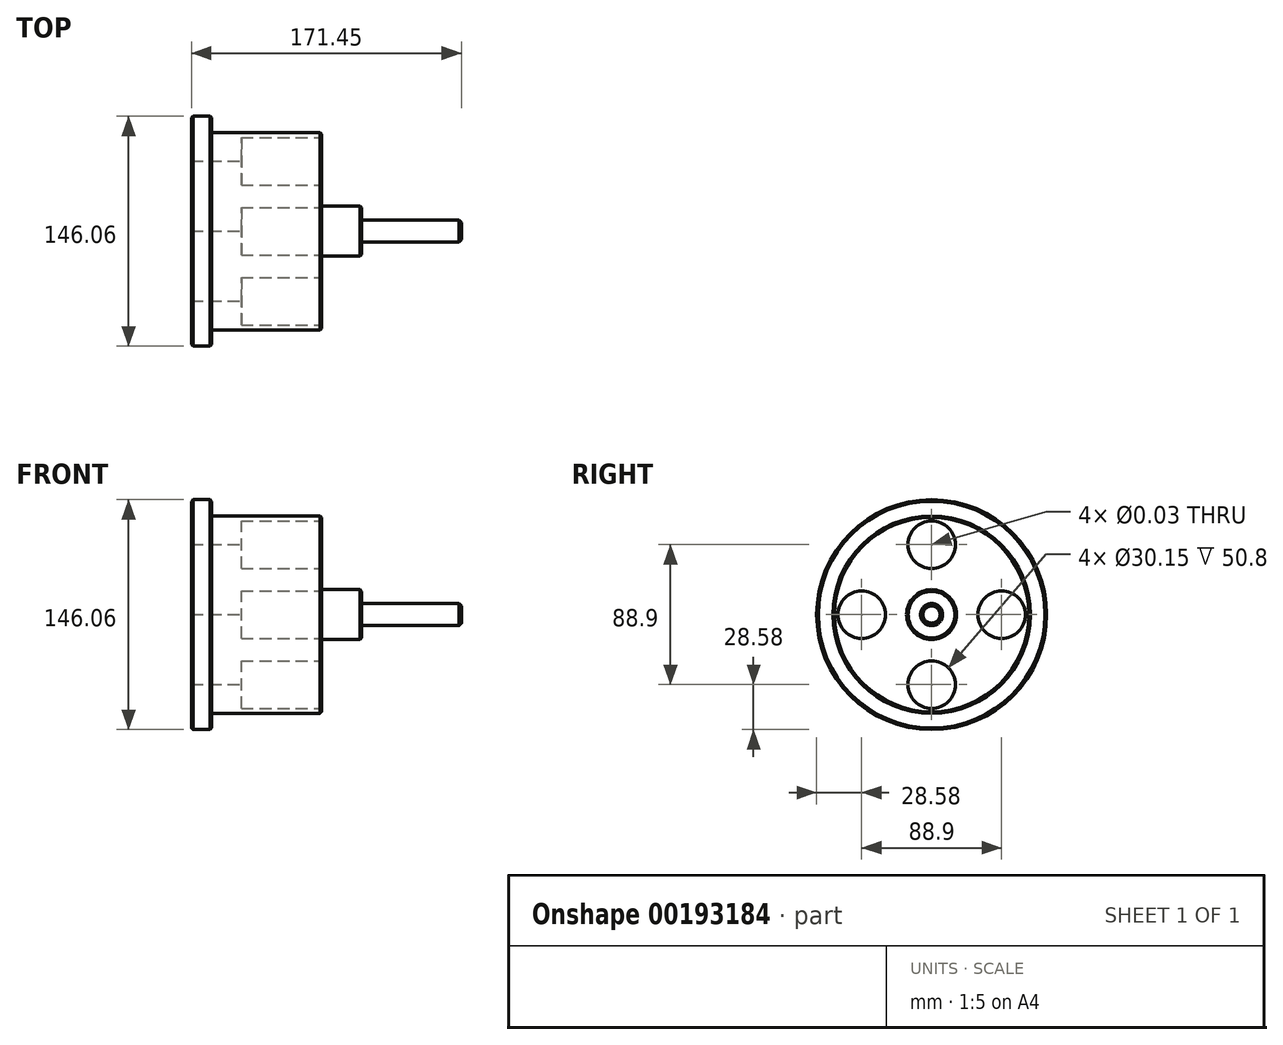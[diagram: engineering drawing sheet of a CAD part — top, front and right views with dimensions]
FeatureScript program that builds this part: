
annotation { "Feature Type Name" : "Feature", "Feature Type Description" : "" }
export const myFeature = defineFeature(function(context is Context, id is Id, definition is map)
    precondition{}
    {
        {
            var Q0;
            Q0=qCreatedBy(makeId("Right.planeOp"),FACE);
            var sketch = newSketch(context, id + "F0", { "sketchPlane" : qUnion([Q0])});
            skCircle(sketch, "E0", {"center": v(0, 0) * mm, "radius": 73.03 * mm});
            skSolve(sketch);
        }
        {
            var Q0;
            Q0 = qSketchRegion(id + "F0", true);
            extrude(context, id + "F1", {"entities" : qUnion([Q0]), "depth" : 12.7 * mm});
        }
        {
            var Q0;
            Q0=makeQuery(id+"F1.opExtrude","CAP_FACE",FACE,{"disambiguationData":[OSD([sQuery(id+"F0.wireOp",EDGE,"E0")])],"isStart":false});
            var sketch = newSketch(context, id + "F2", { "sketchPlane" : qUnion([Q0])});
            skCircle(sketch, "E1", {"center": v(0, 0) * mm, "radius": 62.7 * mm});
            skSolve(sketch);
        }
        {
            var Q0;
            Q0 = qSketchRegion(id + "F2", true);
            extrude(context, id + "F3", {"entities" : qUnion([Q0]), "operationType" : NewBodyOperationType.ADD, "depth" : 69.85 * mm});
        }
        {
            var Q0;
            Q0=makeQuery(id+"F3.opExtrude","CAP_FACE",FACE,{"disambiguationData":[OSD([sQuery(id+"F2.wireOp",EDGE,"E1")])],"isStart":false});
            var sketch = newSketch(context, id + "F4", { "sketchPlane" : qUnion([Q0])});
            skCircle(sketch, "E2", {"center": v(0, 0) * mm, "radius": 15.88 * mm});
            skSolve(sketch);
        }
        {
            var Q0;
            Q0 = qSketchRegion(id + "F4", true);
            extrude(context, id + "F5", {"entities" : qUnion([Q0]), "operationType" : NewBodyOperationType.ADD, "depth" : 25.4 * mm});
        }
        {
            var Q0;
            Q0=makeQuery(id+"F5.opExtrude","CAP_FACE",FACE,{"disambiguationData":[OSD([sQuery(id+"F4.wireOp",EDGE,"E2")])],"isStart":false});
            var sketch = newSketch(context, id + "F6", { "sketchPlane" : qUnion([Q0])});
            skCircle(sketch, "E3", {"center": v(0, 0) * mm, "radius": 7 * mm});
            skSolve(sketch);
        }
        {
            var Q0;
            Q0 = qSketchRegion(id + "F6", true);
            extrude(context, id + "F7", {"entities" : qUnion([Q0]), "operationType" : NewBodyOperationType.ADD, "depth" : 63.5 * mm});
        }
        {
            var Q0;
            Q0=makeQuery(id+"F1.opExtrude","SWEPT_FACE",FACE,{"disambiguationData":[OSD([sQuery(id+"F0.wireOp",EDGE,"E0")])]});
            var Q1;
            Q1=makeQuery(id+"F3.opExtrude","CAP_EDGE",EDGE,{"disambiguationData":[OSD([sQuery(id+"F2.wireOp",EDGE,"E1")])],"isStart":false});
            var Q2;
            Q2=makeQuery(id+"F5.opExtrude","CAP_EDGE",EDGE,{"disambiguationData":[OSD([sQuery(id+"F4.wireOp",EDGE,"E2")])],"isStart":false});
            chamfer(context, id + "F8", {"entities" : qUnion([Q0, Q1, Q2]), "width" : 1.02 * mm, "tangentPropagation" : true});
        }
        {
            var Q0;
            Q0=makeQuery(id+"F7.opExtrude","CAP_EDGE",EDGE,{"disambiguationData":[OSD([sQuery(id+"F6.wireOp",EDGE,"E3")])],"isStart":false});
            chamfer(context, id + "F9", {"entities" : qUnion([Q0]), "width" : 1.52 * mm, "tangentPropagation" : true});
        }
        {
            var Q0;
            Q0=makeQuery(id+"F3.opExtrude","CAP_FACE",FACE,{"disambiguationData":[OSD([sQuery(id+"F2.wireOp",EDGE,"E1")])],"isStart":false});
            var sketch = newSketch(context, id + "F10", { "sketchPlane" : qUnion([Q0])});
            skCircle(sketch, "E4", {"center": v(0, 0) * mm, "radius": 44.45 * mm, "construction": true});
            skLineSegment(sketch, "E5", {"start": v(0, 0) * mm, "end": v(0, 88.67) * mm, "construction": true});
            skPoint(sketch, "E6", {"position": v(0, 44.45) * mm});
            skPoint(sketch, "E7.1.0", {"position": v(-44.45, 0) * mm});
            skPoint(sketch, "E7.2.0", {"position": v(0, -44.45) * mm});
            skPoint(sketch, "E7.3.0", {"position": v(44.45, 0) * mm});
            skSolve(sketch);
        }
        {
            var Q0;
            Q0=sQuery(id+"F10.wireOp",VERTEX,"E6");
            var Q1;
            Q1=sQuery(id+"F10.wireOp",VERTEX,"E7.3.0");
            var Q2;
            Q2=sQuery(id+"F10.wireOp",VERTEX,"E7.2.0");
            var Q3;
            Q3=sQuery(id+"F10.wireOp",VERTEX,"E7.1.0");
            var Q4;
            Q4=makeQuery(id+"F1.opExtrude","SWEPT_BODY",BODY,{"disambiguationData":[OSD([sQuery(id+"F0.wireOp",EDGE,"E0")])]});
            hole(context, id + "F11", {"style" : HoleStyle.C_BORE, "endStyle" : HoleEndStyle.THROUGH, "standardTappedOrClearance" : lookupTablePath({ "standard" : "ANSI", "size" : "13/16 (0.81)", "type" : "Drilled" }), "standardBlindInLast" : lookupTablePath({ "standard" : "ANSI", "size" : "13/16", "type" : "Drilled" }), "holeDiameter" : 13 / 406.4 * mm, "cBoreDiameter" : 30.15 * mm, "cBoreDepth" : 50.8 * mm, "locations" : qUnion([Q0, Q1, Q2, Q3]), "scope" : qUnion([Q4]), "isTappedThrough" : true});
        }
    });
